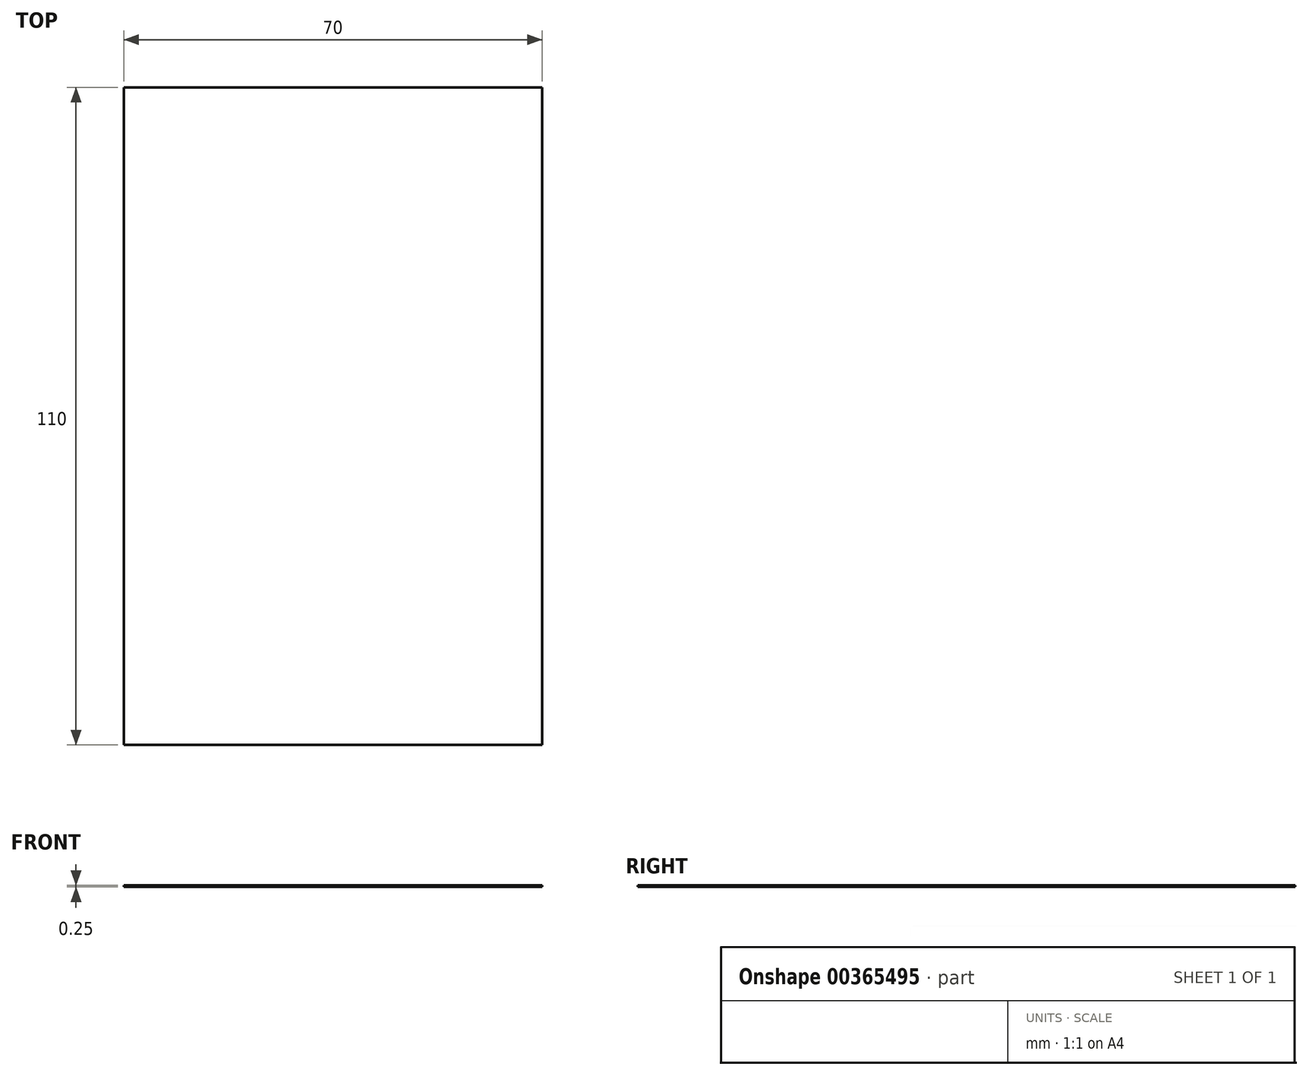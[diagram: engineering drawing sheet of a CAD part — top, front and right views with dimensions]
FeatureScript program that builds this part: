
annotation { "Feature Type Name" : "Feature", "Feature Type Description" : "" }
export const myFeature = defineFeature(function(context is Context, id is Id, definition is map)
    precondition{}
    {
        {
            var Q0;
            Q0=qCreatedBy(makeId("Top.planeOp"),FACE);
            var sketch = newSketch(context, id + "F0", { "sketchPlane" : qUnion([Q0])});
            skLineSegment(sketch, "E0.bottom", {"start": v(35, 55) * mm, "end": v(-35, 55) * mm});
            skLineSegment(sketch, "E0.top", {"start": v(35, -55) * mm, "end": v(-35, -55) * mm});
            skLineSegment(sketch, "E0.left", {"start": v(35, 55) * mm, "end": v(35, -55) * mm});
            skLineSegment(sketch, "E0.right", {"start": v(-35, 55) * mm, "end": v(-35, -55) * mm});
            skPoint(sketch, "E0.middle", {"position": v(0, 0) * mm});
            skSolve(sketch);
        }
        {
            var Q0;
            Q0 = qSketchRegion(id + "F0", true);
            extrude(context, id + "F1", {"entities" : qUnion([Q0]), "depth" : 0.25 * mm});
        }
    });
